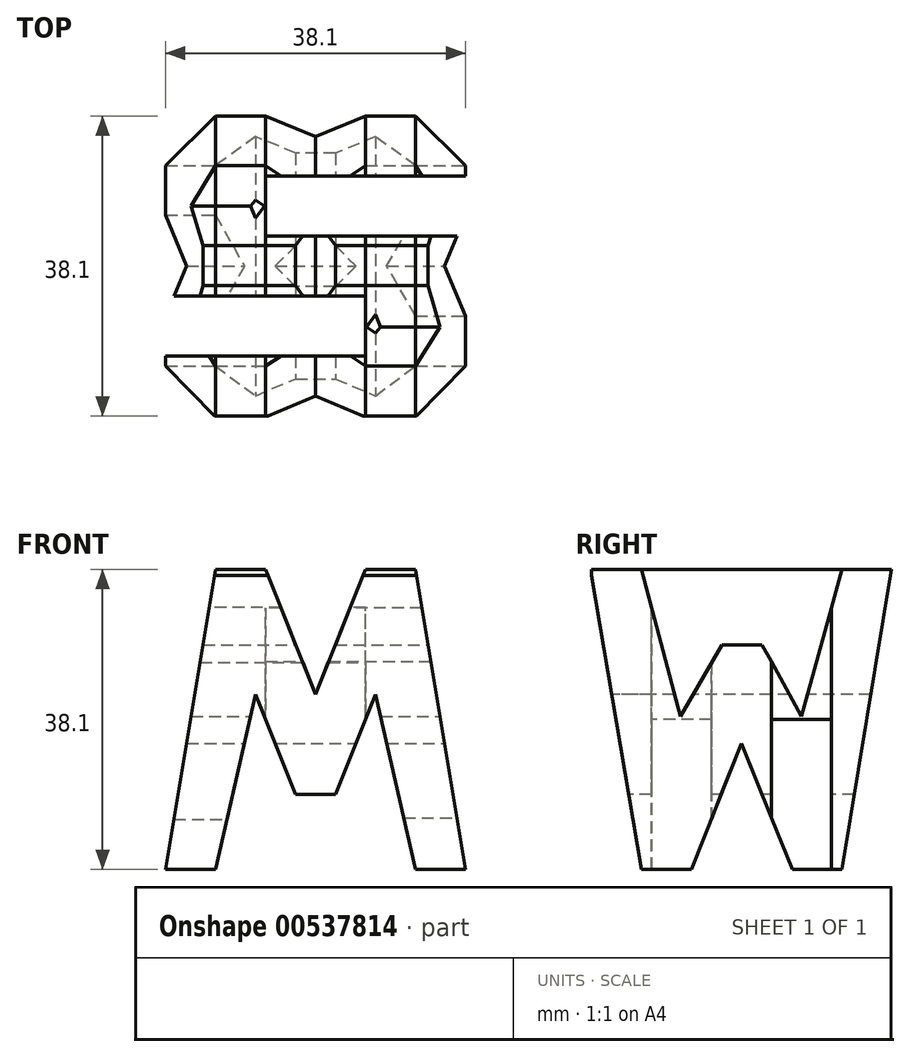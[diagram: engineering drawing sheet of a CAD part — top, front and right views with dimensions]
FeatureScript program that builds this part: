
annotation { "Feature Type Name" : "Feature", "Feature Type Description" : "" }
export const myFeature = defineFeature(function(context is Context, id is Id, definition is map)
    precondition{}
    {
        {
            var Q0;
            Q0=qCreatedBy(makeId("Front.planeOp"),FACE);
            var sketch = newSketch(context, id + "F0", { "sketchPlane" : qUnion([Q0])});
            skLineSegment(sketch, "E0", {"start": v(0, 0) * mm, "end": v(38.1, 0) * mm});
            skLineSegment(sketch, "E1", {"start": v(38.1, 0) * mm, "end": v(38.1, 38.1) * mm});
            skLineSegment(sketch, "E2", {"start": v(38.1, 38.1) * mm, "end": v(0, 38.1) * mm});
            skLineSegment(sketch, "E3", {"start": v(0, 38.1) * mm, "end": v(0, 0) * mm});
            skSolve(sketch);
        }
        {
            var Q0;
            Q0 = qSketchRegion(id + "F0", true);
            extrude(context, id + "F1", {"entities" : qUnion([Q0]), "depth" : 38.1 * mm, "offsetDistance" : 25.4 * mm});
        }
        {
            var Q0;
            Q0=qCreatedBy(makeId("Front.planeOp"),FACE);
            cPlane(context, id + "F2", {"entities" : qUnion([Q0]), "cplaneType" : CPlaneType.OFFSET, "offset" : 38.1 * mm, "width" : 152.4 * mm, "height" : 152.4 * mm});
        }
        {
            var Q0;
            Q0=qCreatedBy(makeId("Right.planeOp"),FACE);
            cPlane(context, id + "F3", {"entities" : qUnion([Q0]), "cplaneType" : CPlaneType.OFFSET, "offset" : 38.1 * mm, "width" : 152.4 * mm, "height" : 152.4 * mm});
        }
        {
            var Q0;
            Q0=qCreatedBy(makeId("Top.planeOp"),FACE);
            cPlane(context, id + "F4", {"entities" : qUnion([Q0]), "cplaneType" : CPlaneType.OFFSET, "offset" : 38.1 * mm, "width" : 152.4 * mm, "height" : 152.4 * mm});
        }
        {
            var Q0;
            Q0=qCreatedBy(id+"F3.planeOp",FACE);
            var sketch = newSketch(context, id + "F5", { "sketchPlane" : qUnion([Q0])});
            skLineSegment(sketch, "E4", {"start": v(0, 38.09) * mm, "end": v(-6.3, 0) * mm});
            skLineSegment(sketch, "E5", {"start": v(-6.3, 0) * mm, "end": v(0, 0) * mm});
            skLineSegment(sketch, "E6", {"start": v(0, 0) * mm, "end": v(0, 38.09) * mm});
            skLineSegment(sketch, "E7", {"start": v(-12.6, 0) * mm, "end": v(-19.07, 16.03) * mm});
            skLineSegment(sketch, "E8", {"start": v(-19.07, 16.03) * mm, "end": v(-25.37, 0) * mm});
            skLineSegment(sketch, "E9", {"start": v(-25.37, 0) * mm, "end": v(-12.6, 0) * mm});
            skLineSegment(sketch, "E10", {"start": v(-31.76, 0) * mm, "end": v(-38.23, 38.09) * mm});
            skLineSegment(sketch, "E11", {"start": v(-38.23, 38.09) * mm, "end": v(-38.23, 0) * mm});
            skLineSegment(sketch, "E12", {"start": v(-38.23, 0) * mm, "end": v(-31.76, 0) * mm});
            skLineSegment(sketch, "E13", {"start": v(-26.82, 19.43) * mm, "end": v(-31.76, 38.09) * mm});
            skLineSegment(sketch, "E14", {"start": v(-31.76, 38.09) * mm, "end": v(-6.3, 38.09) * mm});
            skLineSegment(sketch, "E15", {"start": v(-6.3, 38.09) * mm, "end": v(-11.4, 19.43) * mm});
            skLineSegment(sketch, "E16", {"start": v(-11.4, 19.43) * mm, "end": v(-16.43, 28.55) * mm});
            skLineSegment(sketch, "E17", {"start": v(-16.43, 28.55) * mm, "end": v(-21.54, 28.55) * mm});
            skLineSegment(sketch, "E18", {"start": v(-21.54, 28.55) * mm, "end": v(-26.82, 19.43) * mm});
            skSolve(sketch);
        }
        {
            var Q0;
            Q0 = qSketchRegion(id + "F5", true);
            extrude(context, id + "F6", {"entities" : qUnion([Q0]), "operationType" : NewBodyOperationType.REMOVE, "oppositeDirection" : true, "depth" : 38.1 * mm, "offsetDistance" : 25.4 * mm});
        }
        {
            var Q0;
            Q0=qCreatedBy(id+"F2.planeOp",FACE);
            var sketch = newSketch(context, id + "F7", { "sketchPlane" : qUnion([Q0])});
            skPoint(sketch, "E19", {"position": v(38.1, 0) * mm});
            skPoint(sketch, "E20", {"position": v(38.1, 38.1) * mm});
            skPoint(sketch, "E21", {"position": v(0, 38.1) * mm});
            skLineSegment(sketch, "E22", {"start": v(0, 0) * mm, "end": v(6.35, 38.1) * mm});
            skLineSegment(sketch, "E23", {"start": v(6.35, 38.1) * mm, "end": v(12.7, 38.1) * mm});
            skLineSegment(sketch, "E24", {"start": v(12.7, 38.1) * mm, "end": v(19.05, 22.22) * mm});
            skLineSegment(sketch, "E25", {"start": v(19.05, 22.22) * mm, "end": v(25.4, 38.1) * mm});
            skLineSegment(sketch, "E26", {"start": v(25.4, 38.1) * mm, "end": v(31.75, 38.1) * mm});
            skLineSegment(sketch, "E27", {"start": v(31.75, 38.1) * mm, "end": v(38.1, 0) * mm});
            skLineSegment(sketch, "E28", {"start": v(38.1, 0) * mm, "end": v(31.75, 0) * mm});
            skLineSegment(sketch, "E29", {"start": v(31.75, 0) * mm, "end": v(26.67, 22.23) * mm});
            skLineSegment(sketch, "E30", {"start": v(26.67, 22.23) * mm, "end": v(21.6, 9.52) * mm});
            skLineSegment(sketch, "E31", {"start": v(21.6, 9.52) * mm, "end": v(16.51, 9.52) * mm});
            skLineSegment(sketch, "E32", {"start": v(16.51, 9.52) * mm, "end": v(11.43, 22.22) * mm});
            skLineSegment(sketch, "E33", {"start": v(11.43, 22.23) * mm, "end": v(6.35, 0) * mm});
            skLineSegment(sketch, "E34", {"start": v(6.35, 0) * mm, "end": v(0, 0) * mm});
            skLineSegment(sketch, "E35", {"start": v(0, 0) * mm, "end": v(38.1, 0) * mm});
            skLineSegment(sketch, "E36", {"start": v(38.1, 0) * mm, "end": v(38.1, 38.1) * mm});
            skLineSegment(sketch, "E37", {"start": v(38.1, 38.1) * mm, "end": v(0, 38.1) * mm});
            skLineSegment(sketch, "E38", {"start": v(0, 38.1) * mm, "end": v(0, 0) * mm});
            skSolve(sketch);
        }
        {
            var Q0;
            {var subQ0=sQuery(id+"F7.wireOp",EDGE,"E22");Q0=makeQuery(id+"F7.imprint","IMPRINT",FACE,{"disambiguationData":[TD([[makeQuery(id+"F7.imprint","IMPRINT",EDGE,{"derivedFrom":subQ0}),1.0]])]});}
            var Q1;
            {var subQ0=sQuery(id+"F7.wireOp",EDGE,"E29");Q1=makeQuery(id+"F7.imprint","IMPRINT",FACE,{"disambiguationData":[TD([[makeQuery(id+"F7.imprint","IMPRINT",EDGE,{"derivedFrom":subQ0}),1.0]])]});}
            var Q2;
            {var subQ0=sQuery(id+"F7.wireOp",EDGE,"E24");Q2=makeQuery(id+"F7.imprint","IMPRINT",FACE,{"disambiguationData":[TD([[makeQuery(id+"F7.imprint","IMPRINT",EDGE,{"derivedFrom":subQ0}),1.0]])]});}
            var Q3;
            {var subQ0=sQuery(id+"F7.wireOp",EDGE,"E27");Q3=makeQuery(id+"F7.imprint","IMPRINT",FACE,{"disambiguationData":[TD([[makeQuery(id+"F7.imprint","IMPRINT",EDGE,{"derivedFrom":subQ0}),1.0]])]});}
            extrude(context, id + "F8", {"entities" : qUnion([Q0, Q1, Q2, Q3]), "operationType" : NewBodyOperationType.REMOVE, "oppositeDirection" : true, "depth" : 38.1 * mm, "offsetDistance" : 25.4 * mm});
        }
        {
            var Q0;
            Q0=qCreatedBy(id+"F4.planeOp",FACE);
            var sketch = newSketch(context, id + "F9", { "sketchPlane" : qUnion([Q0])});
            skLineSegment(sketch, "E39", {"start": v(0, 0) * mm, "end": v(38.1, 0) * mm});
            skLineSegment(sketch, "E40", {"start": v(38.1, 0) * mm, "end": v(38.1, -38.1) * mm});
            skLineSegment(sketch, "E41", {"start": v(38.1, -38.1) * mm, "end": v(0, -38.1) * mm});
            skLineSegment(sketch, "E42", {"start": v(0, -38.1) * mm, "end": v(0, 0) * mm});
            skLineSegment(sketch, "E43", {"start": v(38.1, -7.62) * mm, "end": v(12.7, -7.62) * mm});
            skLineSegment(sketch, "E44", {"start": v(12.7, -7.62) * mm, "end": v(12.7, -15.24) * mm});
            skLineSegment(sketch, "E45", {"start": v(12.7, -15.24) * mm, "end": v(38.1, -15.24) * mm});
            skLineSegment(sketch, "E46", {"start": v(0, -22.86) * mm, "end": v(25.4, -22.86) * mm});
            skLineSegment(sketch, "E47", {"start": v(25.4, -22.86) * mm, "end": v(25.4, -30.48) * mm});
            skLineSegment(sketch, "E48", {"start": v(25.4, -30.48) * mm, "end": v(0, -30.48) * mm});
            skSolve(sketch);
        }
        {
            var Q0;
            {var subQ0=sQuery(id+"F9.wireOp",EDGE,"E43");Q0=makeQuery(id+"F9.imprint","IMPRINT",FACE,{"disambiguationData":[TD([[makeQuery(id+"F9.imprint","IMPRINT",EDGE,{"derivedFrom":subQ0}),1.0]])]});}
            var Q1;
            {var subQ0=sQuery(id+"F9.wireOp",EDGE,"E46");Q1=makeQuery(id+"F9.imprint","IMPRINT",FACE,{"disambiguationData":[TD([[makeQuery(id+"F9.imprint","IMPRINT",EDGE,{"derivedFrom":subQ0}),-1.0]])]});}
            extrude(context, id + "F10", {"entities" : qUnion([Q0, Q1]), "operationType" : NewBodyOperationType.REMOVE, "oppositeDirection" : true, "depth" : 38.1 * mm, "offsetDistance" : 25.4 * mm});
        }
        {
            var Q0;
            {var subQ0=makeQuery(id+"F8.opExtrude","SWEPT_FACE",FACE,{"disambiguationData":[OSD([sQuery(id+"F7.wireOp",EDGE,"E22")])]});var subQ1=sQuery(id+"F0.wireOp",EDGE,"E2");var subQ2=makeQuery(id+"F1.opExtrude","SWEPT_FACE",FACE,{"disambiguationData":[OSD([subQ1])]});Q0=makeQuery(id+"F10.boolean.opBoolean","SPLIT",FACE,{"disambiguationData":[TD([makeQuery(id+"F10.opExtrude","SWEPT_FACE",FACE,{"disambiguationData":[OSD([sQuery(id+"F9.wireOp",EDGE,"E43")])]})])],"derivedFrom":makeQuery(id+"F8.boolean.opBoolean","SPLIT",FACE,{"disambiguationData":[TD([subQ0])],"derivedFrom":subQ2})});}
            var Q1;
            {var subQ0=sQuery(id+"F0.wireOp",EDGE,"E2");var subQ1=makeQuery(id+"F1.opExtrude","SWEPT_FACE",FACE,{"disambiguationData":[OSD([subQ0])]});var subQ7=makeQuery(id+"F8.opExtrude","SWEPT_FACE",FACE,{"disambiguationData":[OSD([sQuery(id+"F7.wireOp",EDGE,"E25")])]});Q1=makeQuery(id+"F10.boolean.opBoolean","SPLIT",FACE,{"disambiguationData":[TD([makeQuery(id+"F10.opExtrude","SWEPT_FACE",FACE,{"disambiguationData":[OSD([sQuery(id+"F9.wireOp",EDGE,"E45")])]})])],"derivedFrom":makeQuery(id+"F8.boolean.opBoolean","SPLIT",FACE,{"disambiguationData":[TD([subQ7])],"derivedFrom":subQ1})});}
            extrude(context, id + "F11", {"entities" : qUnion([Q0, Q1]), "operationType" : NewBodyOperationType.REMOVE, "oppositeDirection" : true, "depth" : 0.03 * mm, "offsetDistance" : 25.4 * mm});
        }
    });
